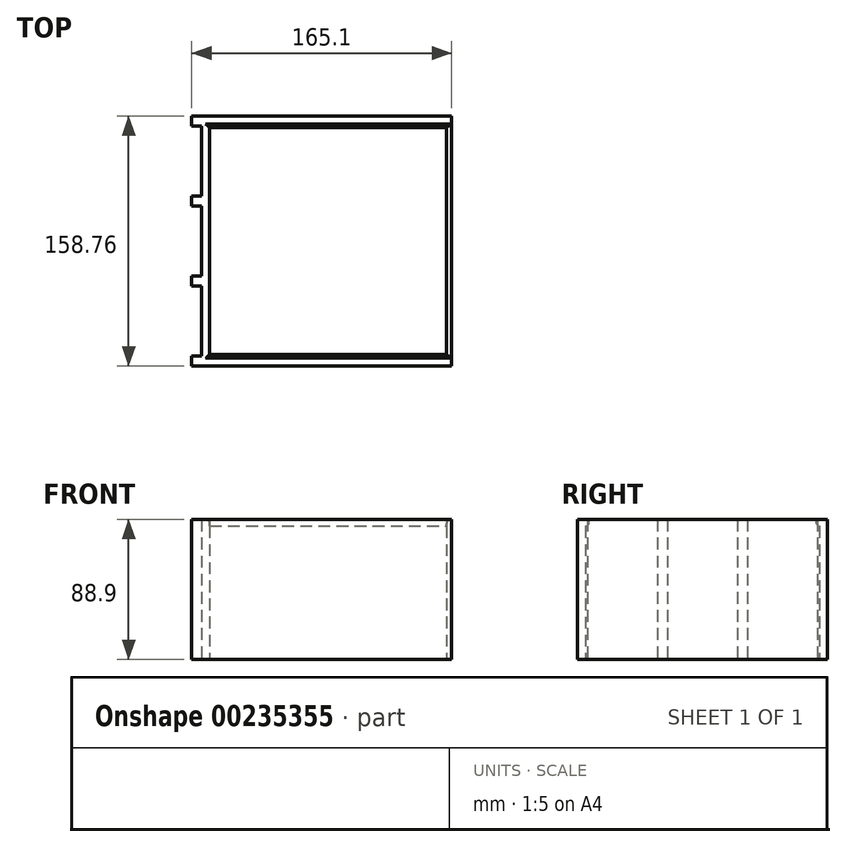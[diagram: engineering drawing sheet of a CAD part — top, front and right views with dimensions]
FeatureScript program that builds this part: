
annotation { "Feature Type Name" : "Feature", "Feature Type Description" : "" }
export const myFeature = defineFeature(function(context is Context, id is Id, definition is map)
    precondition{}
    {
        {
            var Q0;
            Q0=qCreatedBy(makeId("Top.planeOp"),FACE);
            var sketch = newSketch(context, id + "F0", { "sketchPlane" : qUnion([Q0])});
            skLineSegment(sketch, "E0.bottom", {"start": v(-87.64, 53.98) * mm, "end": v(71.1, 53.98) * mm});
            skLineSegment(sketch, "E0.top", {"start": v(-87.64, -104.77) * mm, "end": v(71.1, -104.77) * mm});
            skLineSegment(sketch, "E0.left", {"start": v(-87.64, 53.98) * mm, "end": v(-87.64, -104.77) * mm});
            skLineSegment(sketch, "E0.right", {"start": v(71.1, 53.98) * mm, "end": v(71.1, -104.77) * mm});
            skLineSegment(sketch, "E1.bottom", {"start": v(-94, 53.98) * mm, "end": v(-87.64, 53.98) * mm});
            skLineSegment(sketch, "E1.top", {"start": v(-94, 47.62) * mm, "end": v(-87.64, 47.62) * mm});
            skLineSegment(sketch, "E1.left", {"start": v(-94, 53.98) * mm, "end": v(-94, 47.63) * mm});
            skLineSegment(sketch, "E1.right", {"start": v(-87.64, 53.98) * mm, "end": v(-87.64, 47.63) * mm});
            skLineSegment(sketch, "E2", {"start": v(-91.77, 0) * mm, "end": v(128.93, 0) * mm, "construction": true});
            skLineSegment(sketch, "E3.bottom", {"start": v(-82.56, 48.9) * mm, "end": v(67.93, 48.9) * mm});
            skLineSegment(sketch, "E3.top", {"start": v(-82.56, -99.7) * mm, "end": v(67.93, -99.7) * mm});
            skLineSegment(sketch, "E3.left", {"start": v(-82.56, 48.9) * mm, "end": v(-82.56, -99.7) * mm});
            skLineSegment(sketch, "E3.right", {"start": v(67.93, 48.9) * mm, "end": v(67.93, -99.7) * mm});
            skLineSegment(sketch, "E4.0.1.0", {"start": v(-94, -3.18) * mm, "end": v(-87.64, -3.18) * mm});
            skLineSegment(sketch, "E4.0.1.1", {"start": v(-94, 3.17) * mm, "end": v(-94, -3.17) * mm});
            skLineSegment(sketch, "E4.0.1.2", {"start": v(-94, 3.17) * mm, "end": v(-87.64, 3.17) * mm});
            skLineSegment(sketch, "E4.0.2.0", {"start": v(-94, -53.98) * mm, "end": v(-87.64, -53.98) * mm});
            skLineSegment(sketch, "E4.0.2.1", {"start": v(-94, -47.63) * mm, "end": v(-94, -53.98) * mm});
            skLineSegment(sketch, "E4.0.2.2", {"start": v(-94, -47.63) * mm, "end": v(-87.64, -47.63) * mm});
            skLineSegment(sketch, "E4.0.3.0", {"start": v(-94, -104.78) * mm, "end": v(-87.64, -104.78) * mm});
            skLineSegment(sketch, "E4.0.3.1", {"start": v(-94, -98.43) * mm, "end": v(-94, -104.78) * mm});
            skLineSegment(sketch, "E4.0.3.2", {"start": v(-94, -98.43) * mm, "end": v(-87.64, -98.43) * mm});
            skLineSegment(sketch, "E4.direction1", {"start": v(-94, 47.63) * mm, "end": v(-68.6, 47.63) * mm, "construction": true});
            skLineSegment(sketch, "E4.direction2", {"start": v(-94, 47.63) * mm, "end": v(-94, -3.17) * mm, "construction": true});
            skSolve(sketch);
        }
        {
            var Q0;
            Q0=makeQuery(id+"F0.imprint","IMPRINT",FACE,{"disambiguationData":[TD([[makeQuery(id+"F0.imprint","IMPRINT",EDGE,{"derivedFrom":sQuery(id+"F0.wireOp",EDGE,"E0.bottom")}),-1.0]])]});
            var Q1;
            Q1=makeQuery(id+"F0.imprint","IMPRINT",FACE,{"disambiguationData":[TD([[makeQuery(id+"F0.imprint","IMPRINT",EDGE,{"derivedFrom":sQuery(id+"F0.wireOp",EDGE,"E1.bottom")}),-1.0]])]});
            var Q2;
            {var subQ0=sQuery(id+"F0.wireOp",EDGE,"E4.0.1.0");Q2=makeQuery(id+"F0.imprint","IMPRINT",FACE,{"disambiguationData":[TD([[makeQuery(id+"F0.imprint","IMPRINT",EDGE,{"derivedFrom":subQ0}),1.0]])]});}
            var Q3;
            {var subQ0=sQuery(id+"F0.wireOp",EDGE,"E4.0.2.0");Q3=makeQuery(id+"F0.imprint","IMPRINT",FACE,{"disambiguationData":[TD([[makeQuery(id+"F0.imprint","IMPRINT",EDGE,{"derivedFrom":subQ0}),1.0]])]});}
            var Q4;
            {var subQ0=sQuery(id+"F0.wireOp",EDGE,"E4.0.3.0");Q4=makeQuery(id+"F0.imprint","IMPRINT",FACE,{"disambiguationData":[TD([[makeQuery(id+"F0.imprint","IMPRINT",EDGE,{"derivedFrom":subQ0}),1.0]])]});}
            extrude(context, id + "F1", {"entities" : qUnion([Q0, Q1, Q2, Q3, Q4]), "depth" : 88.9 * mm});
        }
        {
            var Q0;
            Q0=makeQuery(id+"F1.opExtrude","SWEPT_FACE",FACE,{"disambiguationData":[OSD([sQuery(id+"F0.wireOp",EDGE,"E3.left")])]});
            var sketch = newSketch(context, id + "F2", { "sketchPlane" : qUnion([Q0])});
            skCircle(sketch, "E5", {"center": v(48.9, 86.8) * mm, "radius": 2.1 * mm});
            skCircle(sketch, "E6", {"center": v(-99.7, 86.77) * mm, "radius": 2.1 * mm});
            skSolve(sketch);
        }
        {
            var Q0;
            {var subQ0=sQuery(id+"F2.wireOp",EDGE,"E5");var subQ1=makeQuery(id+"F1.opExtrude","SWEPT_EDGE",EDGE,{"disambiguationData":[OSD([sQuery(id+"F0.wireOp",EDGE,"E3.bottom"),sQuery(id+"F0.wireOp",EDGE,"E3.left")])]});var subQ2=makeQuery(id+"F2.imprint","INTERSECT",VERTEX,{"disambiguationData":[OD(0.0)],"derivedFrom":[subQ1,subQ0]});Q0=makeQuery(id+"F2.imprint","IMPRINT",FACE,{"disambiguationData":[TD([[makeQuery(id+"F2.imprint","IMPRINT",EDGE,{"disambiguationData":[TD([[subQ2,1.0]])],"derivedFrom":subQ0}),1.0]])]});}
            var Q1;
            Q1=makeQuery(id+"F1.opExtrude","CAP_EDGE",EDGE,{"disambiguationData":[OSD([sQuery(id+"F0.wireOp",EDGE,"E3.bottom")])],"isStart":false});
            sweep(context, id + "F3", {"operationType" : NewBodyOperationType.ADD, "profiles" : qUnion([Q0]), "path" : qUnion([Q1])});
        }
        {
            var Q0;
            {var subQ0=sQuery(id+"F2.wireOp",EDGE,"E6");var subQ1=makeQuery(id+"F1.opExtrude","SWEPT_EDGE",EDGE,{"disambiguationData":[OSD([sQuery(id+"F0.wireOp",EDGE,"E3.top"),sQuery(id+"F0.wireOp",EDGE,"E3.left")])]});var subQ2=makeQuery(id+"F2.imprint","INTERSECT",VERTEX,{"disambiguationData":[OD(0.0)],"derivedFrom":[subQ1,subQ0]});Q0=makeQuery(id+"F2.imprint","IMPRINT",FACE,{"disambiguationData":[TD([[makeQuery(id+"F2.imprint","IMPRINT",EDGE,{"disambiguationData":[TD([[subQ2,-1.0]])],"derivedFrom":subQ0}),1.0]])]});}
            var Q1;
            Q1=sQuery(id+"F2.wireOp",EDGE,"E6");
            var Q2;
            Q2=makeQuery(id+"F1.opExtrude","CAP_EDGE",EDGE,{"disambiguationData":[OSD([sQuery(id+"F0.wireOp",EDGE,"E3.top")])],"isStart":false});
            sweep(context, id + "F4", {"operationType" : NewBodyOperationType.ADD, "profiles" : qUnion([Q0]), "surfaceProfiles" : qUnion([Q1]), "path" : qUnion([Q2])});
        }
        {
            var Q0;
            Q0=makeQuery(id+"F1.opExtrude","CAP_EDGE",EDGE,{"disambiguationData":[OSD([sQuery(id+"F0.wireOp",EDGE,"E3.left")])],"isStart":false});
            var Q1;
            Q1=makeQuery(id+"F1.opExtrude","CAP_EDGE",EDGE,{"disambiguationData":[OSD([sQuery(id+"F0.wireOp",EDGE,"E3.right")])],"isStart":false});
            fillet(context, id + "F5", {"entities" : qUnion([Q0, Q1]), "radius" : 2.54 * mm, "tangentPropagation" : true, "allowEdgeOverflow" : false});
        }
    });
